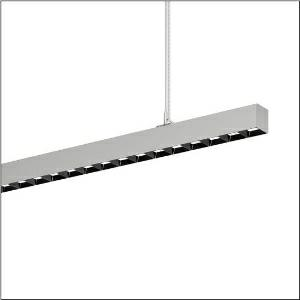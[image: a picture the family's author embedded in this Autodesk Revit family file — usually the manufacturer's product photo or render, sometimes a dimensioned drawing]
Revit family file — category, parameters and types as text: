
# Revit family: silica_r__21_51mx32tat7s_c957
name_source: partatom
category: Lighting Fixtures
units: mm (PartAtom-declared; Revit-internal decimal feet)

## family parameters
Cut with Voids When Loaded = No
Host = Face
Light Source = No
Part Type = Normal
Room Calculation Point = No
Round Connector Dimension = Use Diameter
Shared = No

## types (1)
- --- (1 x LED, 6220 lm, 53.4 W, 6500K)
    Apparent Load = 53 VA
    CIE Flux Codes = 84 99 100 60 100
    Color Rendering = 80
    Color Temperature = 6500K
    Default Elevation = 1800 mm
    Description = Silica® 21, office luminaire, primary light control with darklight reflector, of PMMA, black, CAT 2 (L<= 3000cd/m²), light emission: direct/indirect distribution, primary light characteristic: symmetric, installation type: suspended mounting, LED, rated luminous flux: 6.220lm, luminous efficacy: 111lm/W, light colour: 8tw, colour temperature: 2700..6500K, control gear: ECG DALI, with terminal, 3+2-pole, max. 2.5mm², mains connection: 220..240V, AC, 50/60Hz, rated input power: 56.1W, luminaire housing, of aluminium, metallic grey (RAL 9006), length: 1.204mm, width: 53mm, height: 53mm, protection rating (complete): IP20, insulation class (complete): insulation class I (protective earthing), certification: CE, permissible operating ambient temperature: 0..+35°C, standard: EN 50419, packaging unit: 1 piece
    Height = 53 mm
    Lamp = 1 x LED
    Lamp Light Flux = 6220 lm
    Lamp Power = 53.4 W
    Lamp count = 1
    Length = 1204 mm
    Luminous efficacy = 116 lm/W
    Manufacturer = Siteco
    ModVariant = No
    Model = 51MX32TAT7S
    Mounting Place = Ceiling
    Mounting Type = Pendant
    Number of Poles = 1
    OnlyDefault = Yes
    Power Factor = 1
    Product Name = Silica® 21
    Product group = office luminaire | ceiling pendant
    ProductGroupID = 905
    Protection Class = Protection class I
    Protection Degree = IP 20
    RLX_Detail_Level = 1
    RlxData = <blob elided: 41113 chars, md5=53af9f90>
    Socket = socket
    Standby Power = 0 W
    System Light Flux = 6220 lm
    System Power = 53 W
    Type Comments = individual setting
    Type Image = l_1251731.jpg
    URL = http://relux.com
    VarID = @adj_046017
    Voltage = 0 V
    Weight = 0.00 kg
    Width = 53 mm

## geometry (parser evidence)
native form markers: Blend x4, Sweep x13
no freeform markers — native parametric forms only
